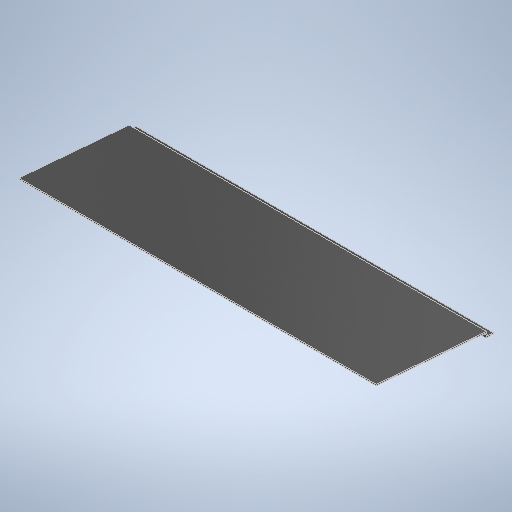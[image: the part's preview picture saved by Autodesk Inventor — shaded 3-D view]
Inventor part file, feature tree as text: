
AUTODESK INVENTOR PART (.ipt)
format: ipt  version: 2025.1 (Build 291241020, 241B)  size: 259,072 bytes
history: native  units: in
note: dims shown in document units (in); Inventor stores cm internally (conversion verified against a paired STEP export)
features: extrude x1, sketch x1
ambient origin geometry x8: Origin, YZ Plane, XZ Plane, XY Plane, X Axis, Y Axis, Z Axis, Center Point
bodies: Body1 (feature_tree)
feature tree (2):
  extrude  "Extrusion2"  Depth=0.125in
  sketch  "Sketch1"  dims[d0=23.408in d1=0.125in d2=0.265in d7=0.125in d8=0.237in d9=1.1431in d10=0.125in d11=0.7449in d12=0.125in d13=12.09in d16=0.125in d18=0.125in d20=12.0907in d21=0.3425in d22=0.125in d23=0.125in d24=0.1549in d25=0.661in d26=39.375in d27=0.0in]
